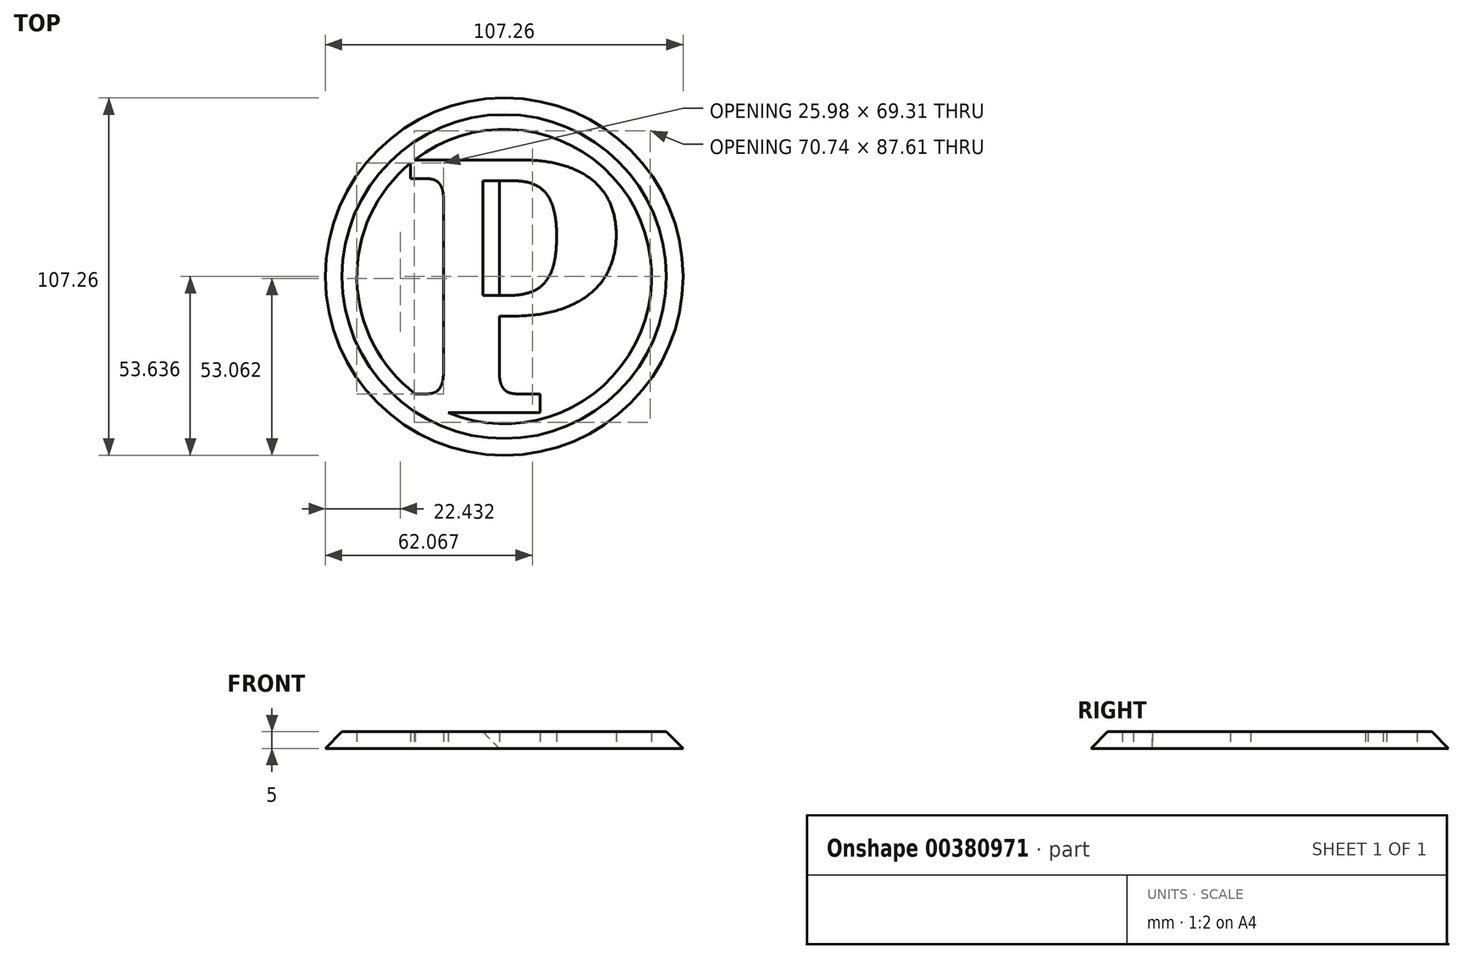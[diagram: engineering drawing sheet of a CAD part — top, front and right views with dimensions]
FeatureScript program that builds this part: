
annotation { "Feature Type Name" : "Feature", "Feature Type Description" : "" }
export const myFeature = defineFeature(function(context is Context, id is Id, definition is map)
    precondition{}
    {
        {
            var Q0;
            Q0=qCreatedBy(makeId("Top.planeOp"),FACE);
            var sketch = newSketch(context, id + "F0", { "sketchPlane" : qUnion([Q0])});
            skCircle(sketch, "E0", {"center": v(0, 0) * mm, "radius": 53.63 * mm});
            skCircle(sketch, "E1", {"center": v(0, 0) * mm, "radius": 44.2 * mm});
            skSolve(sketch);
        }
        {
            var Q0;
            Q0 = qSketchRegion(id + "F0", true);
            extrude(context, id + "F1", {"entities" : qUnion([Q0]), "depth" : 5 * mm});
        }
        {
            var Q0;
            Q0=qCreatedBy(makeId("Top.planeOp"),FACE);
            var sketch = newSketch(context, id + "F2", { "sketchPlane" : qUnion([Q0])});
            skText(sketch, "E2", { "text": "P", "fontName": "NotoSerif-Bold.ttf"});
            const initialGuessF2  = {"E2": [-0.03109, -0.04089, 1, 0, 0.07658]};
            skSetInitialGuess(sketch, initialGuessF2);
            skSolve(sketch);
        }
        {
            var Q0;
            Q0 = qSketchRegion(id + "F2", true);
            extrude(context, id + "F3", {"entities" : qUnion([Q0]), "operationType" : NewBodyOperationType.ADD, "depth" : 5 * mm});
        }
        {
            var Q0;
            Q0=makeQuery(id+"F1.opExtrude","CAP_EDGE",EDGE,{"disambiguationData":[OSD([sQuery(id+"F0.wireOp",EDGE,"E0")])],"isStart":false});
            var Q1;
            Q1=makeQuery(id+"F3.opExtrude","CAP_EDGE",EDGE,{"disambiguationData":[OSD([sQuery(id+"F2.wireOp",EDGE,"E2.sketch_text.stroke-41")])],"isStart":false});
            chamfer(context, id + "F4", {"entities" : qUnion([Q0, Q1]), "width" : 5 * mm, "tangentPropagation" : true});
        }
    });
